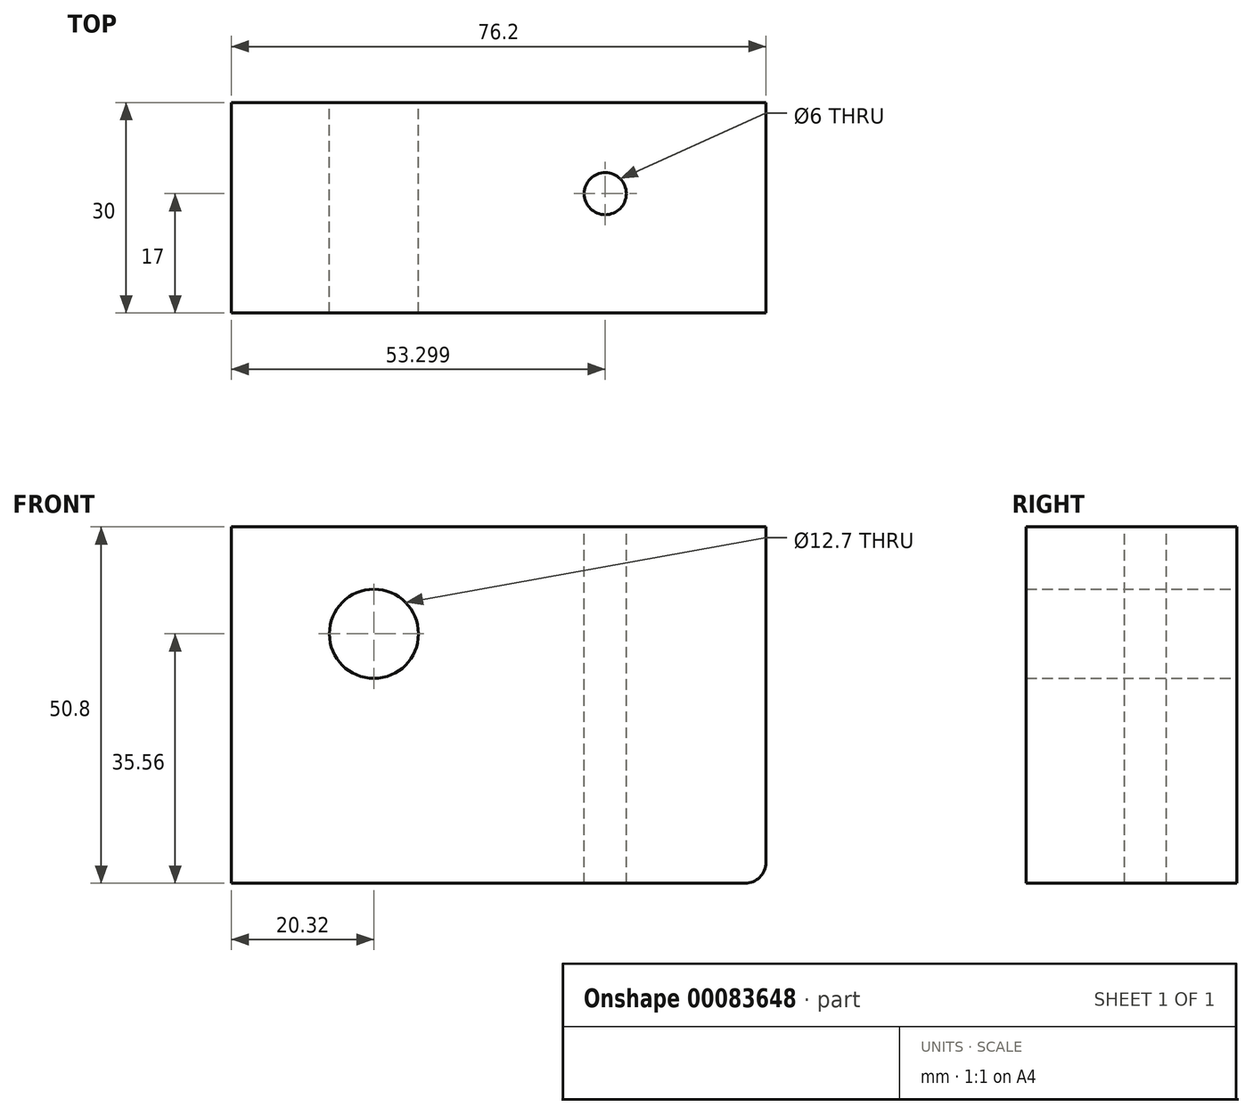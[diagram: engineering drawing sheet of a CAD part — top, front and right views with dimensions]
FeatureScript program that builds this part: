
annotation { "Feature Type Name" : "Feature", "Feature Type Description" : "" }
export const myFeature = defineFeature(function(context is Context, id is Id, definition is map)
    precondition{}
    {
        {
            var Q0;
            Q0=qCreatedBy(makeId("Front.planeOp"),FACE);
            var sketch = newSketch(context, id + "F0", { "sketchPlane" : qUnion([Q0])});
            skLineSegment(sketch, "E0.bottom", {"start": v(-38.1, 25.4) * mm, "end": v(38.1, 25.4) * mm});
            skLineSegment(sketch, "E0.top", {"start": v(-38.1, -25.4) * mm, "end": v(38.1, -25.4) * mm});
            skLineSegment(sketch, "E0.left", {"start": v(-38.1, 25.4) * mm, "end": v(-38.1, -25.4) * mm});
            skLineSegment(sketch, "E0.right", {"start": v(38.1, 25.4) * mm, "end": v(38.1, -25.4) * mm});
            skPoint(sketch, "E0.middle", {"position": v(0, 0) * mm});
            skCircle(sketch, "E1", {"center": v(-17.78, 10.16) * mm, "radius": 6.35 * mm});
            skSolve(sketch);
        }
        {
            var Q0;
            Q0 = qSketchRegion(id + "F0", true);
            extrude(context, id + "F1", {"entities" : qUnion([Q0]), "depth" : 30 * mm});
        }
        {
            var Q0;
            Q0=makeQuery(id+"F1.opExtrude","SWEPT_FACE",FACE,{"disambiguationData":[OSD([sQuery(id+"F0.wireOp",EDGE,"E0.bottom")])]});
            var sketch = newSketch(context, id + "F2", { "sketchPlane" : qUnion([Q0])});
            skCircle(sketch, "E2", {"center": v(15.2, -13) * mm, "radius": 3 * mm});
            skSolve(sketch);
        }
        {
            var Q0;
            Q0 = qSketchRegion(id + "F2", true);
            extrude(context, id + "F3", {"entities" : qUnion([Q0]), "operationType" : NewBodyOperationType.REMOVE, "endBound" : BoundingType.THROUGH_ALL, "oppositeDirection" : true, "depth" : 25 * mm});
        }
        {
            var Q0;
            Q0=makeQuery(id+"F1.opExtrude","SWEPT_EDGE",EDGE,{"disambiguationData":[OSD([sQuery(id+"F0.wireOp",EDGE,"E0.top"),sQuery(id+"F0.wireOp",EDGE,"E0.right")])]});
            fillet(context, id + "F4", {"entities" : qUnion([Q0]), "radius" : 3 * mm, "tangentPropagation" : true, "allowEdgeOverflow" : false});
        }
    });
